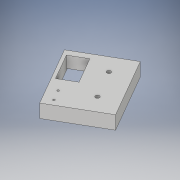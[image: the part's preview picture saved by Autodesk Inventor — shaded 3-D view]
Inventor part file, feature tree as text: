
AUTODESK INVENTOR PART (.ipt)
format: ipt  version: 2017 (Build 210142000, 142)  size: 218,112 bytes
history: native  units: in
note: dims shown in document units (in); Inventor stores cm internally (conversion verified against a paired STEP export)
features: extrude x6, sketch x6, projected_geometry x5, imported_body x1
ambient origin geometry x8: Origin, YZ Plane, XZ Plane, XY Plane, X Axis, Y Axis, Z Axis, Center Point
bodies: Solid1 (feature_tree)
feature tree (18):
  extrude  "Extrusion1"  Depth=0.3937in TaperAngle=0.0deg
  extrude  "Extrusion2"  Depth=0.3937in TaperAngle=0.0deg
  extrude  "Extrusion4"  Depth=0.3937in TaperAngle=0.0deg
  extrude  "Extrusion5"  Depth=0.3937in TaperAngle=0.0deg
  extrude  "Extrusion6"  Depth=0.188in
  extrude  "limit switch"  Depth=0.3937in
  sketch  "Sketch1"  dims[d0=1.25in d1=0.3937in d2=0.0in]
  projected_geometry  "Projected Loop1"
  sketch  "Sketch2"  dims[d3=0.125in d4=0.3937in d5=0.0in]
  sketch  "Sketch4"  dims[d9=0.4331in d10=0.3937in d11=0.0in]
  projected_geometry  "Projected Loop3"
  sketch  "Sketch5"  dims[d12=0.3937in d13=0.3937in d14=0.0in]
  projected_geometry  "Projected Loop4"
  sketch  "Sketch6"  dims[d15=0.765in d16=0.188in]
  projected_geometry  "Projected Loop5"
  sketch  "Sketch7"  dims[d17=0.5in d18=0.125in d19=0.3937in d20=0.0in d21=0.276in d22=0.2in d23=0.575in d24=0.063in d25=0.3937in d26=0.0in]
  projected_geometry  "Projected Loop6"
  imported_body  "Base1"
